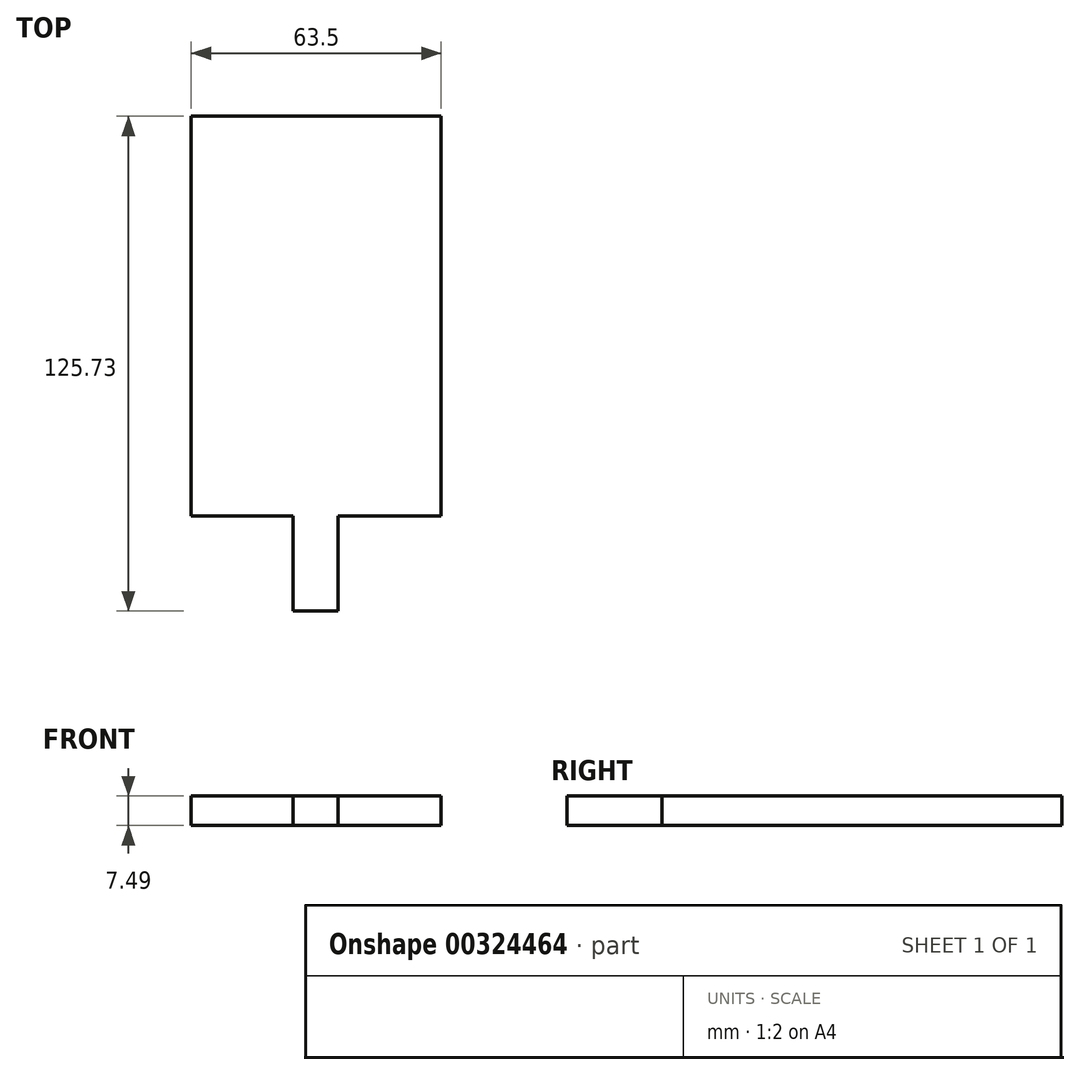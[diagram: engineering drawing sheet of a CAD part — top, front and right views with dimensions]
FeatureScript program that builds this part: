
annotation { "Feature Type Name" : "Feature", "Feature Type Description" : "" }
export const myFeature = defineFeature(function(context is Context, id is Id, definition is map)
    precondition{}
    {
        {
            var Q0;
            Q0=qCreatedBy(makeId("Right.planeOp"),FACE);
            var sketch = newSketch(context, id + "F0", { "sketchPlane" : qUnion([Q0])});
            skLineSegment(sketch, "E0.bottom", {"start": v(0, 0) * mm, "end": v(-101.6, 0) * mm});
            skLineSegment(sketch, "E0.top", {"start": v(0, 7.5) * mm, "end": v(-101.6, 7.5) * mm});
            skLineSegment(sketch, "E0.left", {"start": v(0, 0) * mm, "end": v(0, 7.5) * mm});
            skLineSegment(sketch, "E0.right", {"start": v(-101.6, 0) * mm, "end": v(-101.6, 7.5) * mm});
            skSolve(sketch);
        }
        {
            var Q0;
            Q0 = qSketchRegion(id + "F0", true);
            extrude(context, id + "F1", {"entities" : qUnion([Q0]), "depth" : 63.5 * mm});
        }
        {
            var Q0;
            Q0=makeQuery(id+"F1.opExtrude","SWEPT_FACE",FACE,{"disambiguationData":[OSD([sQuery(id+"F0.wireOp",EDGE,"E0.right")])]});
            var sketch = newSketch(context, id + "F2", { "sketchPlane" : qUnion([Q0])});
            skSolve(sketch);
        }
        {
            var Q0;
            {var subQ0=sQuery(id+"F0.wireOp",EDGE,"E0.right");Q0=makeQuery(id+"F2.imprint","IMPRINT",FACE,{"disambiguationData":[TD([[makeQuery(id+"F2.imprint","IMPRINT",EDGE,{"derivedFrom":makeQuery(id+"F1.opExtrude","CAP_EDGE",EDGE,{"disambiguationData":[OSD([subQ0])],"isStart":true})}),-1.0]])]});}
            var sketch = newSketch(context, id + "F3", { "sketchPlane" : qUnion([Q0])});
            skLineSegment(sketch, "E1.bottom", {"start": v(25.9, 7.5) * mm, "end": v(37.33, 7.5) * mm});
            skLineSegment(sketch, "E1.top", {"start": v(25.9, 0) * mm, "end": v(37.33, 0) * mm});
            skLineSegment(sketch, "E1.left", {"start": v(25.9, 7.5) * mm, "end": v(25.9, 0) * mm});
            skLineSegment(sketch, "E1.right", {"start": v(37.33, 7.5) * mm, "end": v(37.33, 0) * mm});
            skSolve(sketch);
        }
        {
            var Q0;
            Q0=makeQuery(id+"F3.imprint","IMPRINT",FACE,{"disambiguationData":[TD([[makeQuery(id+"F3.imprint","IMPRINT",EDGE,{"derivedFrom":sQuery(id+"F3.wireOp",EDGE,"E1.bottom")}),1.0]])]});
            extrude(context, id + "F4", {"entities" : qUnion([Q0]), "operationType" : NewBodyOperationType.ADD, "depth" : 24.13 * mm});
        }
    });
